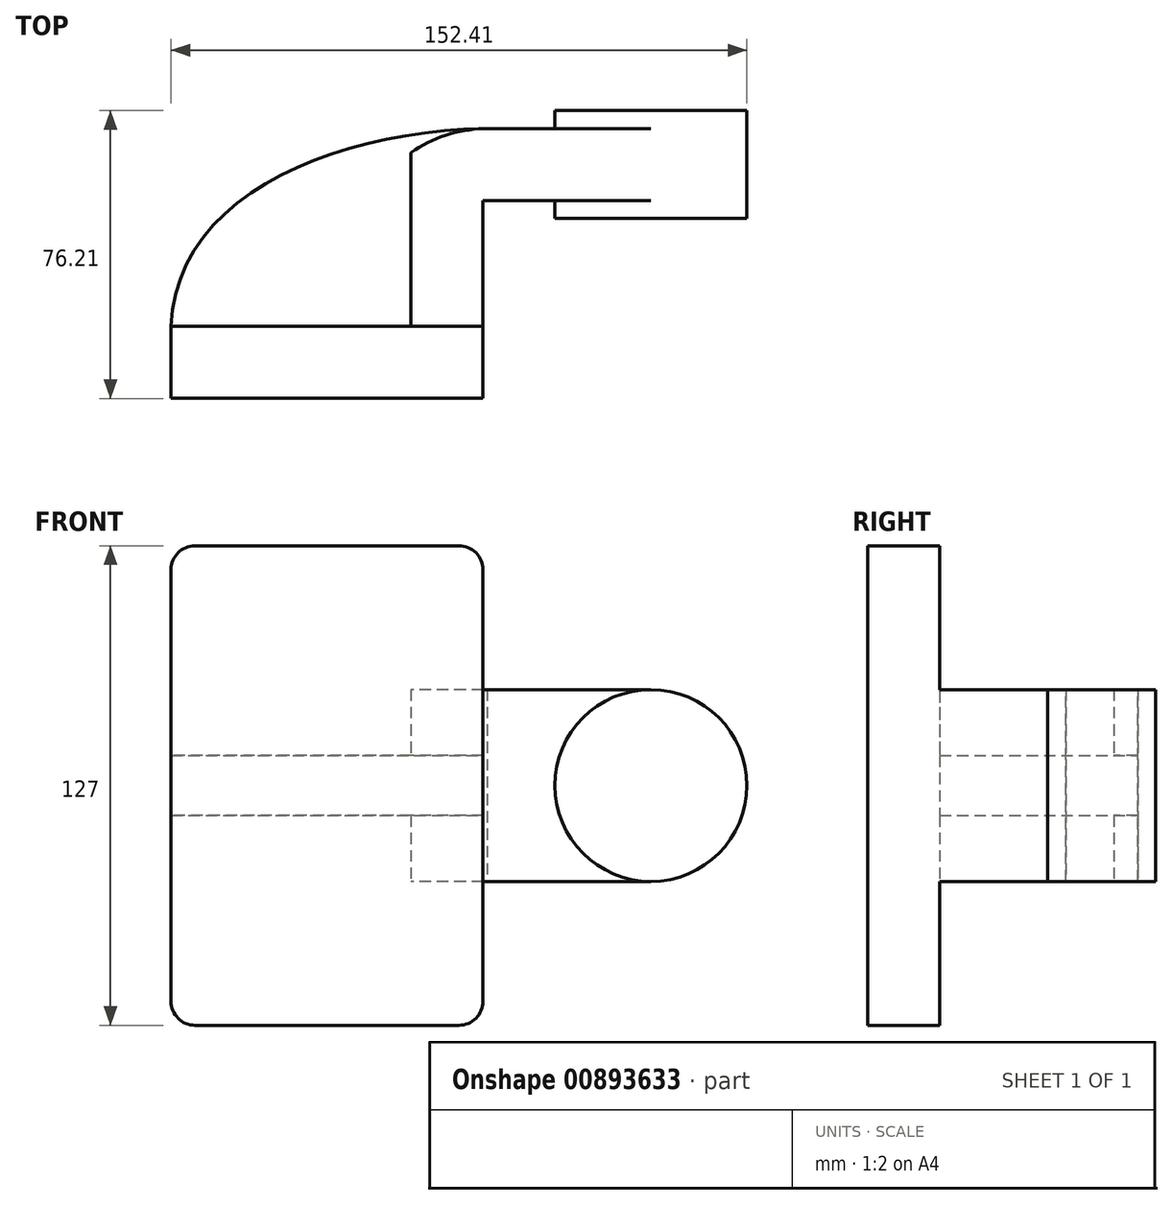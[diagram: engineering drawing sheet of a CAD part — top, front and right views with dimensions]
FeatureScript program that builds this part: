
annotation { "Feature Type Name" : "Feature", "Feature Type Description" : "" }
export const myFeature = defineFeature(function(context is Context, id is Id, definition is map)
    precondition{}
    {
        {
            var Q0;
            Q0=qCreatedBy(makeId("Top.planeOp"),FACE);
            var sketch = newSketch(context, id + "F0", { "sketchPlane" : qUnion([Q0])});
            skLineSegment(sketch, "E0.bottom", {"start": v(41.28, -9.53) * mm, "end": v(-41.28, -9.53) * mm});
            skLineSegment(sketch, "E0.top", {"start": v(41.28, 9.53) * mm, "end": v(-41.28, 9.52) * mm});
            skLineSegment(sketch, "E0.left", {"start": v(41.28, -9.52) * mm, "end": v(41.28, 9.53) * mm});
            skLineSegment(sketch, "E0.right", {"start": v(-41.28, -9.53) * mm, "end": v(-41.28, 9.52) * mm});
            skPoint(sketch, "E0.middle", {"position": v(0, 0) * mm});
            skLineSegment(sketch, "E1", {"start": v(41.28, 9.53) * mm, "end": v(41.28, 42.84) * mm});
            skLineSegment(sketch, "E2.bottom", {"start": v(111.12, 38.1) * mm, "end": v(60.32, 38.1) * mm});
            skLineSegment(sketch, "E2.top", {"start": v(111.12, 66.68) * mm, "end": v(60.32, 66.68) * mm});
            skLineSegment(sketch, "E2.left", {"start": v(111.12, 38.1) * mm, "end": v(111.12, 66.68) * mm});
            skLineSegment(sketch, "E2.right", {"start": v(60.32, 38.1) * mm, "end": v(60.32, 66.68) * mm});
            skPoint(sketch, "E2.middle", {"position": v(85.72, 52.39) * mm});
            skLineSegment(sketch, "E3", {"start": v(42.36, 42.88) * mm, "end": v(85.72, 42.88) * mm});
            skPoint(sketch, "E3.endSnap0", {"position": v(85.72, 38.1) * mm});
            skArc(sketch, "E4", {"start": v(42.36, 42.88) * mm, "mid": v(41.82, 42.87) * mm, "end": v(41.28, 42.84) * mm});
            skLineSegment(sketch, "E5.0", {"start": v(42.36, 61.93) * mm, "end": v(85.72, 61.93) * mm});
            skArc(sketch, "E5.1", {"start": v(42.36, 61.93) * mm, "mid": v(31.8, 60.29) * mm, "end": v(22.23, 55.54) * mm});
            skLineSegment(sketch, "E5.2", {"start": v(22.23, 9.53) * mm, "end": v(22.23, 55.54) * mm});
            skLineSegment(sketch, "E6", {"start": v(85.72, 38.1) * mm, "end": v(85.72, 66.68) * mm});
            skFitSpline(sketch, "E7", {"points": [v(-41.28, 9.52) * mm, v(42.36, 61.93) * mm], "startDerivative": vector(3.54, 104.98) * mm, "endDerivative": vector(118.9, 1.28) * mm});
            skSolve(sketch);
        }
        {
            var Q0;
            Q0=makeQuery(id+"F0.imprint","IMPRINT",FACE,{"disambiguationData":[TD([[makeQuery(id+"F0.imprint","IMPRINT",EDGE,{"derivedFrom":sQuery(id+"F0.wireOp",EDGE,"E0.bottom")}),-1.0]])]});
            extrude(context, id + "F1", {"entities" : qUnion([Q0]), "endBound" : BoundingType.SYMMETRIC, "depth" : 127 * mm, "offsetDistance" : 25.4 * mm});
        }
        {
            var Q0;
            {var subQ6=sQuery(id+"F0.wireOp",EDGE,"E1");Q0=makeQuery(id+"F0.imprint","IMPRINT",FACE,{"disambiguationData":[TD([[makeQuery(id+"F0.imprint","IMPRINT",EDGE,{"derivedFrom":subQ6}),1.0]])]});}
            var Q1;
            {var subQ0=sQuery(id+"F0.wireOp",EDGE,"E3");var subQ1=sQuery(id+"F0.wireOp",EDGE,"E2.right");var subQ2=makeQuery(id+"F0.imprint","INTERSECT",VERTEX,{"derivedFrom":[subQ1,subQ0]});Q1=makeQuery(id+"F0.imprint","IMPRINT",FACE,{"disambiguationData":[TD([[makeQuery(id+"F0.imprint","IMPRINT",EDGE,{"disambiguationData":[TD([[subQ2,-1.0]])],"derivedFrom":subQ1}),-1.0]])]});}
            extrude(context, id + "F2", {"entities" : qUnion([Q0, Q1]), "operationType" : NewBodyOperationType.ADD, "endBound" : BoundingType.SYMMETRIC, "depth" : 50.8 * mm, "offsetDistance" : 25.4 * mm});
        }
        {
            var Q0;
            {var subQ3=sQuery(id+"F0.wireOp",EDGE,"E5.2");Q0=makeQuery(id+"F0.imprint","IMPRINT",FACE,{"disambiguationData":[TD([[makeQuery(id+"F0.imprint","IMPRINT",EDGE,{"derivedFrom":subQ3}),1.0]])]});}
            extrude(context, id + "F3", {"entities" : qUnion([Q0]), "operationType" : NewBodyOperationType.ADD, "endBound" : BoundingType.SYMMETRIC, "depth" : 15.88 * mm, "offsetDistance" : 25.4 * mm});
        }
        {
            var Q0;
            Q0=makeQuery(id+"F1.opExtrude","CAP_EDGE",EDGE,{"disambiguationData":[OSD([sQuery(id+"F0.wireOp",EDGE,"E0.left")])],"isStart":false});
            var Q1;
            Q1=makeQuery(id+"F1.opExtrude","CAP_EDGE",EDGE,{"disambiguationData":[OSD([sQuery(id+"F0.wireOp",EDGE,"E0.right")])],"isStart":false});
            var Q2;
            Q2=makeQuery(id+"F1.opExtrude","CAP_EDGE",EDGE,{"disambiguationData":[OSD([sQuery(id+"F0.wireOp",EDGE,"E0.right")])],"isStart":true});
            var Q3;
            Q3=makeQuery(id+"F1.opExtrude","CAP_EDGE",EDGE,{"disambiguationData":[OSD([sQuery(id+"F0.wireOp",EDGE,"E0.left")])],"isStart":true});
            fillet(context, id + "F4", {"entities" : qUnion([Q0, Q1, Q2, Q3]), "radius" : 6.35 * mm, "tangentPropagation" : true, "allowEdgeOverflow" : false});
        }
        {
            var Q0;
            {var subQ4=sQuery(id+"F0.wireOp",EDGE,"E2.left");Q0=makeQuery(id+"F0.imprint","IMPRINT",FACE,{"disambiguationData":[TD([[makeQuery(id+"F0.imprint","IMPRINT",EDGE,{"derivedFrom":subQ4}),1.0]])]});}
            var Q1;
            Q1=sQuery(id+"F0.wireOp",EDGE,"E6");
            revolve(context, id + "F5", {"operationType" : NewBodyOperationType.ADD, "surfaceOperationType" : NewSurfaceOperationType.NEW, "entities" : qUnion([Q0]), "axis" : qUnion([Q1]), "revolveType" : RevolveType.FULL});
        }
    });
